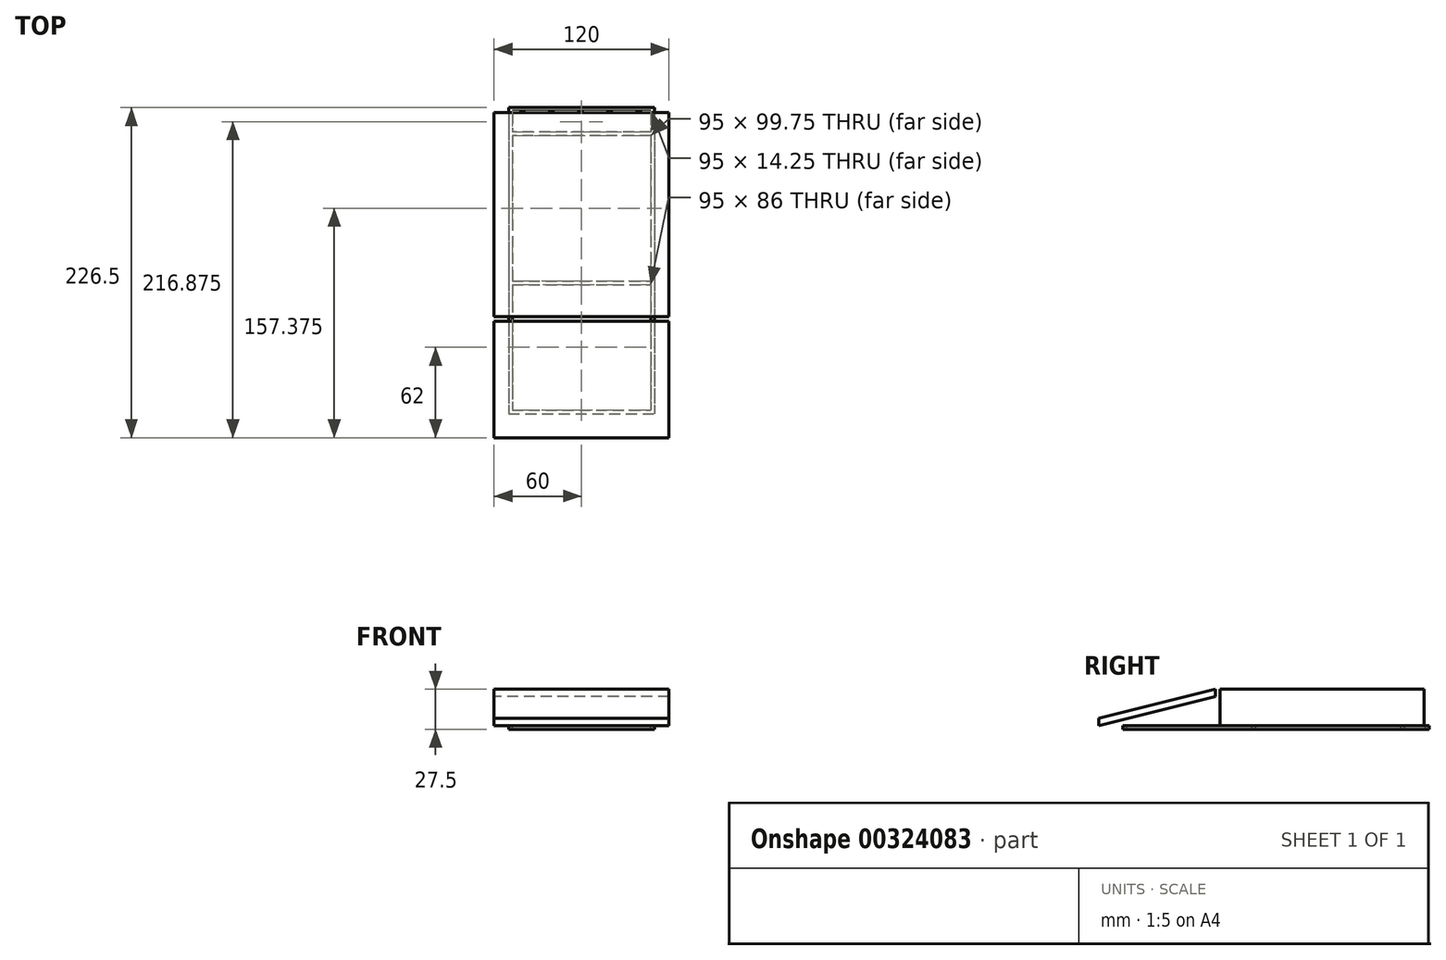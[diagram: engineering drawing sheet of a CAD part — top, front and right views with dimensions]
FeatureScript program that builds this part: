
annotation { "Feature Type Name" : "Feature", "Feature Type Description" : "" }
export const myFeature = defineFeature(function(context is Context, id is Id, definition is map)
    precondition{}
    {
        {
            var Q0;
            Q0=qCreatedBy(makeId("Top.planeOp"),FACE);
            var sketch = newSketch(context, id + "F0", { "sketchPlane" : qUnion([Q0])});
            skLineSegment(sketch, "E0.bottom", {"start": v(-50, 121.5) * mm, "end": v(50, 121.5) * mm});
            skLineSegment(sketch, "E0.top", {"start": v(-50, 0) * mm, "end": v(50, 0) * mm});
            skLineSegment(sketch, "E0.left", {"start": v(-50, 121.5) * mm, "end": v(-50, 0) * mm});
            skLineSegment(sketch, "E0.right", {"start": v(50, 121.5) * mm, "end": v(50, 0) * mm});
            skLineSegment(sketch, "E1.0", {"start": v(-47.5, 119) * mm, "end": v(47.5, 119) * mm});
            skLineSegment(sketch, "E1.1", {"start": v(-47.5, 119) * mm, "end": v(-47.5, 2.5) * mm});
            skLineSegment(sketch, "E1.2", {"start": v(-47.5, 2.5) * mm, "end": v(47.5, 2.5) * mm});
            skLineSegment(sketch, "E1.3", {"start": v(47.5, 119) * mm, "end": v(47.5, 2.5) * mm});
            skLineSegment(sketch, "E2", {"start": v(-50, 60.75) * mm, "end": v(50, 60.75) * mm, "construction": true});
            skLineSegment(sketch, "E3", {"start": v(50, 18) * mm, "end": v(-50, 18) * mm, "construction": true});
            skLineSegment(sketch, "E4", {"start": v(0, -23.5) * mm, "end": v(0, 133.06) * mm, "construction": true});
            skPoint(sketch, "E4.endSnap0", {"position": v(0, 121.5) * mm});
            skLineSegment(sketch, "E5.MirrorCS", {"start": v(50, 103.5) * mm, "end": v(-50, 103.5) * mm, "construction": true});
            skLineSegment(sketch, "E6.bottom", {"start": v(47.5, 102.25) * mm, "end": v(-47.5, 102.25) * mm});
            skLineSegment(sketch, "E6.top", {"start": v(47.5, 104.75) * mm, "end": v(-47.5, 104.75) * mm});
            skLineSegment(sketch, "E6.left", {"start": v(47.5, 102.25) * mm, "end": v(47.5, 104.75) * mm});
            skLineSegment(sketch, "E6.right", {"start": v(-47.5, 102.25) * mm, "end": v(-47.5, 104.75) * mm});
            skPoint(sketch, "E6.middle", {"position": v(0, 103.5) * mm});
            skLineSegment(sketch, "E7.direction1", {"start": v(-47.5, 104.75) * mm, "end": v(-22.5, 104.75) * mm, "construction": true});
            skLineSegment(sketch, "E7.direction2", {"start": v(-47.5, 104.75) * mm, "end": v(-47.5, 74.38) * mm, "construction": true});
            skLineSegment(sketch, "E8.top", {"start": v(-50, -88.5) * mm, "end": v(50, -88.5) * mm});
            skLineSegment(sketch, "E8.left", {"start": v(-50, 0) * mm, "end": v(-50, -88.5) * mm});
            skLineSegment(sketch, "E8.right", {"start": v(50, 0) * mm, "end": v(50, -88.5) * mm});
            skLineSegment(sketch, "E9.top", {"start": v(-47.5, -86) * mm, "end": v(47.5, -86) * mm});
            skLineSegment(sketch, "E9.left", {"start": v(-47.5, 2.5) * mm, "end": v(-47.5, -86) * mm});
            skLineSegment(sketch, "E9.right", {"start": v(47.5, 2.5) * mm, "end": v(47.5, -86) * mm});
            skLineSegment(sketch, "E10.bottom", {"start": v(-60, 118) * mm, "end": v(60, 118) * mm});
            skLineSegment(sketch, "E10.top", {"start": v(-60, -22) * mm, "end": v(60, -22) * mm});
            skLineSegment(sketch, "E10.left", {"start": v(-60, 118) * mm, "end": v(-60, -22) * mm});
            skLineSegment(sketch, "E10.right", {"start": v(60, 118) * mm, "end": v(60, -22) * mm});
            skLineSegment(sketch, "E11.bottom", {"start": v(-60, -25) * mm, "end": v(60, -25) * mm});
            skLineSegment(sketch, "E11.top", {"start": v(-60, -105) * mm, "end": v(60, -105) * mm});
            skLineSegment(sketch, "E11.left", {"start": v(-60, -25) * mm, "end": v(-60, -105) * mm});
            skLineSegment(sketch, "E11.right", {"start": v(60, -25) * mm, "end": v(60, -105) * mm});
            skLineSegment(sketch, "E12", {"start": v(0, -25) * mm, "end": v(0, -116.17) * mm, "construction": true});
            skSolve(sketch);
        }
        {
            var Q0;
            {var subQ1=sQuery(id+"F0.wireOp",EDGE,"E1.1");var subQ6=makeQuery(id+"F0.imprint","INTERSECT",VERTEX,{"derivedFrom":[subQ1,sQuery(id+"F0.wireOp",EDGE,"E6.bottom")]});Q0=makeQuery(id+"F0.imprint","IMPRINT",FACE,{"disambiguationData":[TD([[makeQuery(id+"F0.imprint","IMPRINT",EDGE,{"disambiguationData":[TD([[subQ6,1.0]])],"derivedFrom":subQ1}),-1.0]])]});}
            var Q1;
            {var subQ2=sQuery(id+"F0.wireOp",EDGE,"E0.bottom");Q1=makeQuery(id+"F0.imprint","IMPRINT",FACE,{"disambiguationData":[TD([[makeQuery(id+"F0.imprint","IMPRINT",EDGE,{"derivedFrom":subQ2}),-1.0]])]});}
            var Q2;
            {var subQ0=sQuery(id+"F0.wireOp",EDGE,"E6.bottom");Q2=makeQuery(id+"F0.imprint","IMPRINT",FACE,{"disambiguationData":[TD([[makeQuery(id+"F0.imprint","IMPRINT",EDGE,{"derivedFrom":subQ0}),-1.0]])]});}
            var Q3;
            {var subQ1=sQuery(id+"F0.wireOp",EDGE,"E1.3");var subQ11=makeQuery(id+"F0.imprint","INTERSECT",VERTEX,{"derivedFrom":[subQ1,sQuery(id+"F0.wireOp",EDGE,"E6.bottom")]});Q3=makeQuery(id+"F0.imprint","IMPRINT",FACE,{"disambiguationData":[TD([[makeQuery(id+"F0.imprint","IMPRINT",EDGE,{"disambiguationData":[TD([[subQ11,1.0]])],"derivedFrom":subQ1}),1.0]])]});}
            var Q4;
            {var subQ5=sQuery(id+"F0.wireOp",EDGE,"E1.2");Q4=makeQuery(id+"F0.imprint","IMPRINT",FACE,{"disambiguationData":[TD([[makeQuery(id+"F0.imprint","IMPRINT",EDGE,{"derivedFrom":subQ5}),-1.0]])]});}
            var Q5;
            {var subQ0=sQuery(id+"F0.wireOp",EDGE,"E9.left");var subQ1=sQuery(id+"F0.wireOp",EDGE,"E0.top");var subQ2=makeQuery(id+"F0.imprint","INTERSECT",VERTEX,{"derivedFrom":[subQ1,subQ0]});Q5=makeQuery(id+"F0.imprint","IMPRINT",FACE,{"disambiguationData":[TD([[makeQuery(id+"F0.imprint","IMPRINT",EDGE,{"disambiguationData":[TD([[subQ2,-1.0]])],"derivedFrom":subQ0}),-1.0]])]});}
            var Q6;
            {var subQ1=sQuery(id+"F0.wireOp",EDGE,"E8.top");Q6=makeQuery(id+"F0.imprint","IMPRINT",FACE,{"disambiguationData":[TD([[makeQuery(id+"F0.imprint","IMPRINT",EDGE,{"derivedFrom":subQ1}),1.0]])]});}
            var Q7;
            {var subQ3=sQuery(id+"F0.wireOp",EDGE,"E9.right");var subQ5=sQuery(id+"F0.wireOp",EDGE,"E10.top");var subQ6=makeQuery(id+"F0.imprint","INTERSECT",VERTEX,{"derivedFrom":[subQ3,subQ5]});Q7=makeQuery(id+"F0.imprint","IMPRINT",FACE,{"disambiguationData":[TD([[makeQuery(id+"F0.imprint","IMPRINT",EDGE,{"disambiguationData":[TD([[subQ6,1.0]])],"derivedFrom":subQ3}),1.0]])]});}
            var Q8;
            {var subQ0=sQuery(id+"F0.wireOp",EDGE,"E11.bottom");var subQ1=sQuery(id+"F0.wireOp",EDGE,"E8.left");var subQ2=makeQuery(id+"F0.imprint","INTERSECT",VERTEX,{"derivedFrom":[subQ1,subQ0]});Q8=makeQuery(id+"F0.imprint","IMPRINT",FACE,{"disambiguationData":[TD([[makeQuery(id+"F0.imprint","IMPRINT",EDGE,{"disambiguationData":[TD([[subQ2,1.0]])],"derivedFrom":subQ1}),1.0]])]});}
            var Q9;
            {var subQ0=sQuery(id+"F0.wireOp",EDGE,"E11.bottom");var subQ1=sQuery(id+"F0.wireOp",EDGE,"E8.right");var subQ2=makeQuery(id+"F0.imprint","INTERSECT",VERTEX,{"derivedFrom":[subQ1,subQ0]});Q9=makeQuery(id+"F0.imprint","IMPRINT",FACE,{"disambiguationData":[TD([[makeQuery(id+"F0.imprint","IMPRINT",EDGE,{"disambiguationData":[TD([[subQ2,1.0]])],"derivedFrom":subQ1}),-1.0]])]});}
            extrude(context, id + "F1", {"entities" : qUnion([Q0, Q1, Q2, Q3, Q4, Q5, Q6, Q7, Q8, Q9]), "oppositeDirection" : true, "depth" : 2.5 * mm, "offsetDistance" : 25 * mm});
        }
        {
            var Q0;
            {var subQ0=sQuery(id+"F0.wireOp",EDGE,"E9.left");var subQ1=sQuery(id+"F0.wireOp",EDGE,"E0.top");var subQ2=makeQuery(id+"F0.imprint","INTERSECT",VERTEX,{"derivedFrom":[subQ1,subQ0]});Q0=makeQuery(id+"F0.imprint","IMPRINT",FACE,{"disambiguationData":[TD([[makeQuery(id+"F0.imprint","IMPRINT",EDGE,{"disambiguationData":[TD([[subQ2,-1.0]])],"derivedFrom":subQ0}),-1.0]])]});}
            var Q1;
            {var subQ0=sQuery(id+"F0.wireOp",EDGE,"E9.left");var subQ1=sQuery(id+"F0.wireOp",EDGE,"E0.top");var subQ2=makeQuery(id+"F0.imprint","INTERSECT",VERTEX,{"derivedFrom":[subQ1,subQ0]});Q1=makeQuery(id+"F0.imprint","IMPRINT",FACE,{"disambiguationData":[TD([[makeQuery(id+"F0.imprint","IMPRINT",EDGE,{"disambiguationData":[TD([[subQ2,-1.0]])],"derivedFrom":subQ1}),-1.0]])]});}
            var Q2;
            {var subQ3=sQuery(id+"F0.wireOp",EDGE,"E9.right");var subQ5=sQuery(id+"F0.wireOp",EDGE,"E10.top");var subQ6=makeQuery(id+"F0.imprint","INTERSECT",VERTEX,{"derivedFrom":[subQ3,subQ5]});Q2=makeQuery(id+"F0.imprint","IMPRINT",FACE,{"disambiguationData":[TD([[makeQuery(id+"F0.imprint","IMPRINT",EDGE,{"disambiguationData":[TD([[subQ6,1.0]])],"derivedFrom":subQ3}),1.0]])]});}
            var Q3;
            {var subQ3=sQuery(id+"F0.wireOp",EDGE,"E10.right");Q3=makeQuery(id+"F0.imprint","IMPRINT",FACE,{"disambiguationData":[TD([[makeQuery(id+"F0.imprint","IMPRINT",EDGE,{"derivedFrom":subQ3}),-1.0]])]});}
            var Q4;
            {var subQ5=sQuery(id+"F0.wireOp",EDGE,"E1.2");Q4=makeQuery(id+"F0.imprint","IMPRINT",FACE,{"disambiguationData":[TD([[makeQuery(id+"F0.imprint","IMPRINT",EDGE,{"derivedFrom":subQ5}),-1.0]])]});}
            var Q5;
            {var subQ1=sQuery(id+"F0.wireOp",EDGE,"E1.3");var subQ11=makeQuery(id+"F0.imprint","INTERSECT",VERTEX,{"derivedFrom":[subQ1,sQuery(id+"F0.wireOp",EDGE,"E6.bottom")]});Q5=makeQuery(id+"F0.imprint","IMPRINT",FACE,{"disambiguationData":[TD([[makeQuery(id+"F0.imprint","IMPRINT",EDGE,{"disambiguationData":[TD([[subQ11,1.0]])],"derivedFrom":subQ1}),1.0]])]});}
            var Q6;
            {var subQ1=sQuery(id+"F0.wireOp",EDGE,"E1.1");var subQ6=makeQuery(id+"F0.imprint","INTERSECT",VERTEX,{"derivedFrom":[subQ1,sQuery(id+"F0.wireOp",EDGE,"E6.bottom")]});Q6=makeQuery(id+"F0.imprint","IMPRINT",FACE,{"disambiguationData":[TD([[makeQuery(id+"F0.imprint","IMPRINT",EDGE,{"disambiguationData":[TD([[subQ6,1.0]])],"derivedFrom":subQ1}),-1.0]])]});}
            var Q7;
            {var subQ0=sQuery(id+"F0.wireOp",EDGE,"E6.bottom");Q7=makeQuery(id+"F0.imprint","IMPRINT",FACE,{"disambiguationData":[TD([[makeQuery(id+"F0.imprint","IMPRINT",EDGE,{"derivedFrom":subQ0}),-1.0]])]});}
            var Q8;
            {var subQ5=sQuery(id+"F0.wireOp",EDGE,"E10.left");Q8=makeQuery(id+"F0.imprint","IMPRINT",FACE,{"disambiguationData":[TD([[makeQuery(id+"F0.imprint","IMPRINT",EDGE,{"derivedFrom":subQ5}),1.0]])]});}
            var Q9;
            {var subQ2=sQuery(id+"F0.wireOp",EDGE,"E1.2");Q9=makeQuery(id+"F0.imprint","IMPRINT",FACE,{"disambiguationData":[TD([[makeQuery(id+"F0.imprint","IMPRINT",EDGE,{"derivedFrom":subQ2}),1.0]])]});}
            var Q10;
            {var subQ3=sQuery(id+"F0.wireOp",EDGE,"E6.top");Q10=makeQuery(id+"F0.imprint","IMPRINT",FACE,{"disambiguationData":[TD([[makeQuery(id+"F0.imprint","IMPRINT",EDGE,{"derivedFrom":subQ3}),-1.0]])]});}
            extrude(context, id + "F2", {"entities" : qUnion([Q0, Q1, Q2, Q3, Q4, Q5, Q6, Q7, Q8, Q9, Q10]), "depth" : 25 * mm, "offsetDistance" : 25 * mm});
        }
        {
            var Q0;
            {var subQ4=sQuery(id+"F0.wireOp",EDGE,"E8.top");Q0=makeQuery(id+"F0.imprint","IMPRINT",FACE,{"disambiguationData":[TD([[makeQuery(id+"F0.imprint","IMPRINT",EDGE,{"derivedFrom":subQ4}),-1.0]])]});}
            var Q1;
            {var subQ2=sQuery(id+"F0.wireOp",EDGE,"E8.top");Q1=makeQuery(id+"F0.imprint","IMPRINT",FACE,{"disambiguationData":[TD([[makeQuery(id+"F0.imprint","IMPRINT",EDGE,{"derivedFrom":subQ2}),1.0]])]});}
            var Q2;
            {var subQ0=sQuery(id+"F0.wireOp",EDGE,"E9.top");Q2=makeQuery(id+"F0.imprint","IMPRINT",FACE,{"disambiguationData":[TD([[makeQuery(id+"F0.imprint","IMPRINT",EDGE,{"derivedFrom":subQ0}),1.0]])]});}
            extrude(context, id + "F3", {"entities" : qUnion([Q0, Q1, Q2]), "depth" : 25 * mm, "offsetDistance" : 25 * mm});
        }
        {
            var Q0;
            Q0=makeQuery(id+"F3.opExtrude","CAP_EDGE",EDGE,{"disambiguationData":[OSD([sQuery(id+"F0.wireOp",EDGE,"E11.top")])],"isStart":false});
            var Q1;
            Q1=makeQuery(id+"F3.opExtrude","CAP_EDGE",EDGE,{"disambiguationData":[OSD([sQuery(id+"F0.wireOp",EDGE,"E11.bottom")])],"isStart":true});
            chamfer(context, id + "F4", {"entities" : qUnion([Q0, Q1]), "chamferType" : ChamferType.TWO_OFFSETS, "width1" : 80 * mm, "oppositeDirection" : false, "width2" : 20 * mm, "tangentPropagation" : true});
        }
    });
